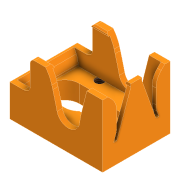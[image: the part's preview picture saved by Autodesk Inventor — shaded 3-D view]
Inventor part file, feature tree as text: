
AUTODESK INVENTOR PART (.ipt)
format: ipt  version: 2021 (Build 250183000, 183)  size: 733,184 bytes
history: native  units: mm
features: sketch x27, extrude x26, projected_geometry x24, chamfer x15, fillet x15, move_body x6, direct_edit x5, other x3, mirror x2, hole x1, delete_face x1, reference x1
ambient origin geometry x8: Origin, YZ Plane, XZ Plane, XY Plane, X Axis, Y Axis, Z Axis, Center Point
bodies: Volumenkörper1 (feature_tree)
feature tree (126):
  extrude  "Extrusion1"  Depth=16.1mm
  extrude  "Extrusion2"  Depth=19.1mm
  extrude  "Extrusion3"  Depth=5.8mm
  extrude  "Extrusion4"  Depth=3.5mm
  extrude  "Extrusion5"  Depth=14.5mm
  chamfer  "Fase1"  [1 undecoded]
  fillet  "Rundung1"  Radius=8.0mm
  mirror  "Spiegeln1"
  extrude  "Extrusion6"  Depth=8.0mm
  mirror  "Spiegeln2"
  extrude  "Extrusion7"  Depth=2.5mm
  chamfer  "Fase2"  Distance=2.0mm
  extrude  "Extrusion8"  Depth=1.5mm
  chamfer  "Fase3"  Distance=2.0mm
  fillet  "Rundung2"  Radius=0.5mm
  fillet  "Rundung3"  Radius=3.65mm
  extrude  "Extrusion9"  Depth=1.5mm
  extrude  "Extrusion10"  Depth=6.0mm
  extrude  "Extrusion11"  Depth=2.0mm TaperAngle=0.0deg
  fillet  "Rundung4"  Radius=12.0mm
  fillet  "Rundung5"  Radius=3.0mm
  extrude  "Extrusion12"  Depth=4.0mm TaperAngle=0.0deg
  hole  "Bohrung1"  [1 undecoded]
  extrude  "Extrusion13"  Depth=0.8mm
  extrude  "Extrusion14"  Depth=3.5mm
  extrude  "Extrusion15"  Depth=2.0mm TaperAngle=0.0deg
  chamfer  "Fase4"  Distance=0.5mm
  fillet  "Rundung6"  Radius=1.0mm
  fillet  "Rundung7"  Radius=1.0mm
  extrude  "Extrusion16"  Depth=1.5mm TaperAngle=0.0deg
  extrude  "Extrusion17"  TaperAngle=0.0deg  [1 undecoded]
  extrude  "Extrusion18"  Depth=10.0mm
  fillet  "Rundung8"  Radius=5.6mm
  fillet  "Rundung9"  Radius=1.5mm
  extrude  "Extrusion19"  Depth=10.0mm
  extrude  "Extrusion20"  Depth=0.4mm
  fillet  "Rundung10"  Radius=14.5mm
  extrude  "Extrusion21"  Depth=10.0mm TaperAngle=0.0deg
  chamfer  "Fase5"  Distance=0.05mm
  chamfer  "Fase6"  Distance=5.0mm
  chamfer  "Fase7"  [1 undecoded]
  chamfer  "Fase8"  Distance=99.0mm
  chamfer  "Fase9"  Distance=99.0mm
  extrude  "Extrusion22"  Depth=0.4mm TaperAngle=0.0deg
  fillet  "Rundung13"  Radius=2.0mm
  chamfer  "Fase10"  Distance=4.0mm
  chamfer  "Fase11"  Distance=2.0mm
  fillet  "Rundung14"  Radius=3.0mm
  delete_face  "Fläche löschen1"
  extrude  "Extrusion23"  Depth=0.4mm
  extrude  "Extrusion24"  Depth=0.4mm
  direct_edit  "Direktbearbeitung1"
  direct_edit  "Direktbearbeitung2"
  direct_edit  "Direktbearbeitung3"
  extrude  "Extrusion25"  Depth=1.1mm
  direct_edit  "Direktbearbeitung4"
  extrude  "Extrusion26"  Depth=1.1mm
  chamfer  "Fase12"  Distance=0.1mm
  fillet  "Rundung15"  Radius=5.0mm
  chamfer  "Fase13"  Distance=1.0mm
  chamfer  "Fase14"  Distance=1.0mm
  fillet  "Rundung16"  Radius=10.0mm
  fillet  "Rundung17"  Radius=15.3mm
  direct_edit  "Direktbearbeitung5"
  chamfer  "Fase15"  Distance=16.1mm
  sketch  "Skizze1"  dims[d0=23.1mm d1=16.1mm]
  sketch  "Skizze2"  dims[d2=26.1mm d3=19.1mm]
  sketch  "Skizze3"  dims[d4=13.1mm d5=0.0mm d8=5.8mm]
  projected_geometry  "Projizierte Kontur1"
  sketch  "Skizze4"  dims[d9=90.0deg d10=3.5mm]
  projected_geometry  "Projizierte Kontur2"
  sketch  "Skizze5"  dims[d11=2.0mm d12=14.5mm]
  sketch  "Skizze6"  dims[d13=0.0mm]
  sketch  "Skizze7"  dims[d14=4.25mm]
  sketch  "Skizze8"  dims[d15=90.0deg]
  sketch  "Skizze9"  dims[d16=6.5mm d17=0.0mm d18=0.0mm d19=8.0mm]
  sketch  "Skizze10"  dims[d20=0.0mm d21=8.0mm]
  projected_geometry  "Projizierte Kontur3"
  sketch  "Skizze11"  dims[d22=2.5mm d23=5.9mm d24=2.0mm d25=0.0mm]
  projected_geometry  "Projizierte Kontur4"
  sketch  "Skizze12"  dims[d26=0.0mm d27=0.0mm d28=1.5mm d29=2.0mm d30=0.0mm]
  projected_geometry  "Projizierte Kontur5"
  sketch  "Skizze13"  dims[d31=1.2mm d32=2.0mm d33=45.0deg d34=0.5mm d35=3.65mm]
  sketch  "Skizze15"  dims[d36=180.0deg d37=1.5mm]
  reference  "Referenz4"
  projected_geometry  "Projizierte Kontur6"
  sketch  "Skizze16"  dims[d38=2.0mm d39=0.0mm d40=6.0mm]
  projected_geometry  "Projizierte Kontur7"
  sketch  "Skizze17"  dims[d41=3.0mm d42=2.0mm d43=0.0mm]
  projected_geometry  "Projizierte Kontur8"
  sketch  "Skizze18"  dims[d44=1.2mm d45=2.0mm d46=45.0deg d47=12.0mm d48=3.0mm]
  projected_geometry  "Projizierte Kontur9"
  projected_geometry  "Projizierte Kontur10"
  sketch  "Skizze19"  dims[d49=4.0mm d50=2.0mm d51=0.0mm]
  projected_geometry  "Projizierte Kontur11"
  projected_geometry  "Projizierte Kontur12"
  sketch  "Skizze20"  dims[d52=1.2mm d53=2.0mm d54=45.0deg d55=0.5mm]
  projected_geometry  "Projizierte Kontur13"
  sketch  "Skizze21"  dims[d56=0.8mm d57=3.5mm]
  projected_geometry  "Projizierte Kontur14"
  projected_geometry  "Projizierte Kontur15"
  sketch  "Skizze22"  dims[d58=2.0mm d59=3.5mm]
  projected_geometry  "Projizierte Kontur16"
  projected_geometry  "Projizierte Kontur17"
  sketch  "Skizze23"  dims[d60=2.0mm d61=2.0mm d62=0.0mm]
  projected_geometry  "Projizierte Kontur18"
  sketch  "Skizze24"  dims[d63=3.0mm d64=0.5mm d65=0.0mm d66=1.0mm d67=0.0mm d68=1.0mm]
  projected_geometry  "Projizierte Kontur19"
  sketch  "Skizze25"  dims[d69=3.0mm d70=1.5mm d71=0.0mm]
  sketch  "Skizze26"  dims[d72=2.459mm d73=6.0mm d74=6.5mm d75=3.0mm d76=90.0deg d77=6.0mm d78=0.0mm d79=0.0mm d80=0.0mm]
  projected_geometry  "Projizierte Kontur20"
  projected_geometry  "Projizierte Kontur21"
  sketch  "Skizze27"  dims[d81=0.0mm d82=0.0mm d83=10.0mm d84=5.6mm d85=1.5mm d86=0.0mm]
  projected_geometry  "Projizierte Kontur22"
  projected_geometry  "Projizierte Kontur23"
  sketch  "Skizze28"  dims[d87=2.0mm d88=2.0mm d89=11.717774mm d90=10.0mm d91=1.0mm d92=14.5mm d93=10.0mm d94=0.0mm d95=0.05mm d96=0.0mm d97=5.0mm d98=0.0mm d99=0.0mm d100=99.0mm d101=99.0mm d102=1.91mm d103=0.0mm d104=2.0mm d105=0.0mm d106=4.0mm d107=2.0mm d108=0.0mm d109=3.0mm d110=2.0mm d111=4.537856mm d113=0.5mm d114=1.0mm d115=4.537856mm d116=0.5mm d117=1.0mm d118=4.537856mm d119=1.1mm d120=1.0mm d121=4.537856mm d122=1.1mm d123=1.0mm d124=4.537856mm d126=0.1mm d127=0.0mm d128=5.0mm d129=1.0mm d130=2.0mm d131=4.537856mm d132=1.0mm d133=2.0mm d134=4.537856mm d135=10.0mm d136=15.3mm d137=16.1mm d138=2.0mm d139=0.0mm d140=0.3mm d141=0.0mm d142=0.0mm d143=0.0mm d144=-0.4mm d145=0.0mm d146=0.0mm d147=-0.2mm d148=0.0mm d149=0.0mm d150=-0.4mm d151=6.5mm d152=6.5mm d153=3.1mm d154=0.8mm d155=0.8mm d156=0.4mm d157=0.0mm d158=0.0mm d159=0.0mm d160=-0.4mm d161=4.0mm d162=2.0mm d163=4.0mm d164=2.0mm d165=0.0mm d167=0.8mm d168=0.8mm d169=0.8mm d170=4.0mm d171=0.0mm d172=2.5mm d173=2.0mm d174=45.0deg d175=5.0mm d176=2.0mm d177=8.0mm d178=45.0deg d179=2.0mm d180=8.0mm d181=45.0deg d182=1.2mm d183=20.0mm d184=0.0mm d185=0.0mm d186=-0.1mm d187=0.0mm d188=0.0mm d189=-0.1mm d190=0.4mm d191=2.0mm d192=45.0deg]
  projected_geometry  "Projizierte Kontur24"
  other  "<userpath>\Desktop\DragonHF\Combined.iam"
  other  "Combined.iam"
  other  "AdxlMount:1"
  move_body  "Verschieben1"
  move_body  "Verschieben2"
  move_body  "Verschieben3"
  move_body  "Verschieben4"
  move_body  "Verschieben5"
  move_body  "Verschieben6"
note: 4 required parameter values undecoded (feature->parameter linkage not recoverable at this tier; creation-order binding heuristic only, values carry confidence <= 0.55)
